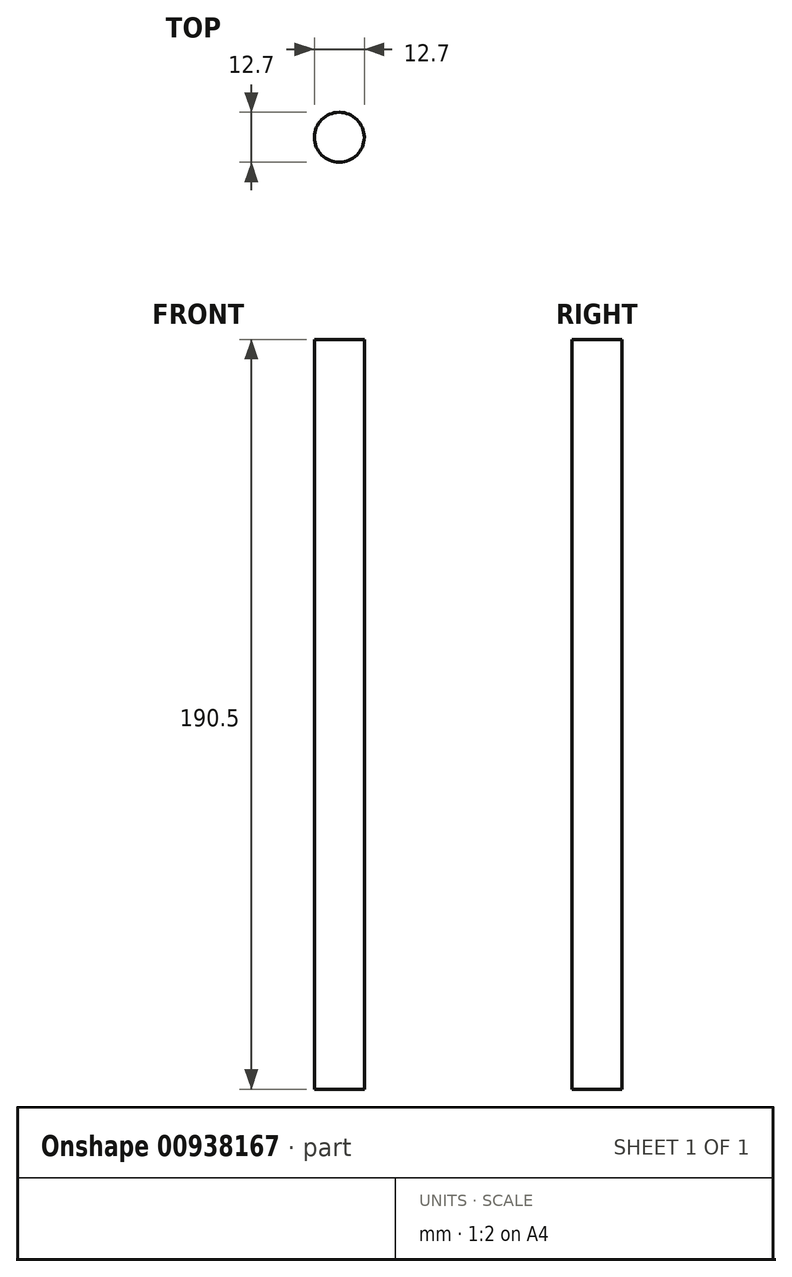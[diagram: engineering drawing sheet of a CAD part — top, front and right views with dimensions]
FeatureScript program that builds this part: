
annotation { "Feature Type Name" : "Feature", "Feature Type Description" : "" }
export const myFeature = defineFeature(function(context is Context, id is Id, definition is map)
    precondition{}
    {
        {
            var Q0;
            Q0=qCreatedBy(makeId("Top.planeOp"),FACE);
            var sketch = newSketch(context, id + "F0", { "sketchPlane" : qUnion([Q0])});
            skCircle(sketch, "E0", {"center": v(-75.98, 39.37) * mm, "radius": 6.35 * mm});
            skSolve(sketch);
        }
        {
            var Q0;
            Q0=makeQuery(id+"F0.imprint","IMPRINT",FACE,{"disambiguationData":[TD([[makeQuery(id+"F0.imprint","IMPRINT",EDGE,{"derivedFrom":sQuery(id+"F0.wireOp",EDGE,"E0")}),1.0]])]});
            extrude(context, id + "F1", {"entities" : qUnion([Q0]), "depth" : 190.5 * mm, "offsetDistance" : 25 * mm});
        }
    });
